# Revit family: Door_Impact_SuperSeal_1500Series
name_source: partatom
category: Doors
revit_build: Autodesk Revit Architecture 2012 (Build: 20110309_2315(x64)
units: mm (PartAtom-declared; Revit-internal decimal feet)

## types (1)
- ByType
    ADA Compliant = Yes
    Construction Details = http://arcat.com
    Description = Super Seal
    Door Width = 3' - 0"
    Edge Channels = Yes
    Expected Lifespan (Years) = 0
    Fire Rating = As Specified
    Frame Thickness = 0' - 4 3/4"
    Function = Interior
    Gasketed = No
    Glass Type = Plastic - Acrylic - Super Seal - Clear
    Hardware Finish = Metal - Stainless Steel - Super Seal - Brushed
    Height = 7' - 0"
    Keynote = 08300
    Maintenance Schedule (Months) = 0
    Manufacturer = Super-Seal Mfg. Ltd
    Manufacturer Fax = 905-850-4440
    Manufacturer Website = http://www.supersealmfg.com
    Model = As Specified
    Panel Height = 6' - 0"
    Panel Material = Metal - Aluminum - Super Seal - Anodized - Brown
    Panel Width = 2' - 0"
    Product Data = http://arcat.com
    Protector Material = Rubber - Super Seal - Black
    RO Offset = 0' - 0 1/2"
    R_Value = 0
    Rough Height = 7' - 0 1/2"
    Rough Width = 6' - 1"
    Sales Information = http://www.supersealmfg.com
    Seal Material = Rubber - Super Seal - Black
    Send Message = http://www.arcat.com &mf=
    Sound Transmission Class (STC) = 0
    Stile Width = 0' - 5 1/8"
    Thickness = 0' - 0 1/2"
    URL = http://www.supersealmfg.com
    Vision Panel Frame Material = Rubber - Super Seal - Black
    Vision Panel Height = 1' - 2"
    Vision Panel Width = 0' - 9"
    Wall Closure = By host
    Warranty Duration (Years) = 0
    Width = 6' - 0"

## geometry (parser evidence)
native form markers: Blend x24, Sweep x4
no freeform markers — native parametric forms only
